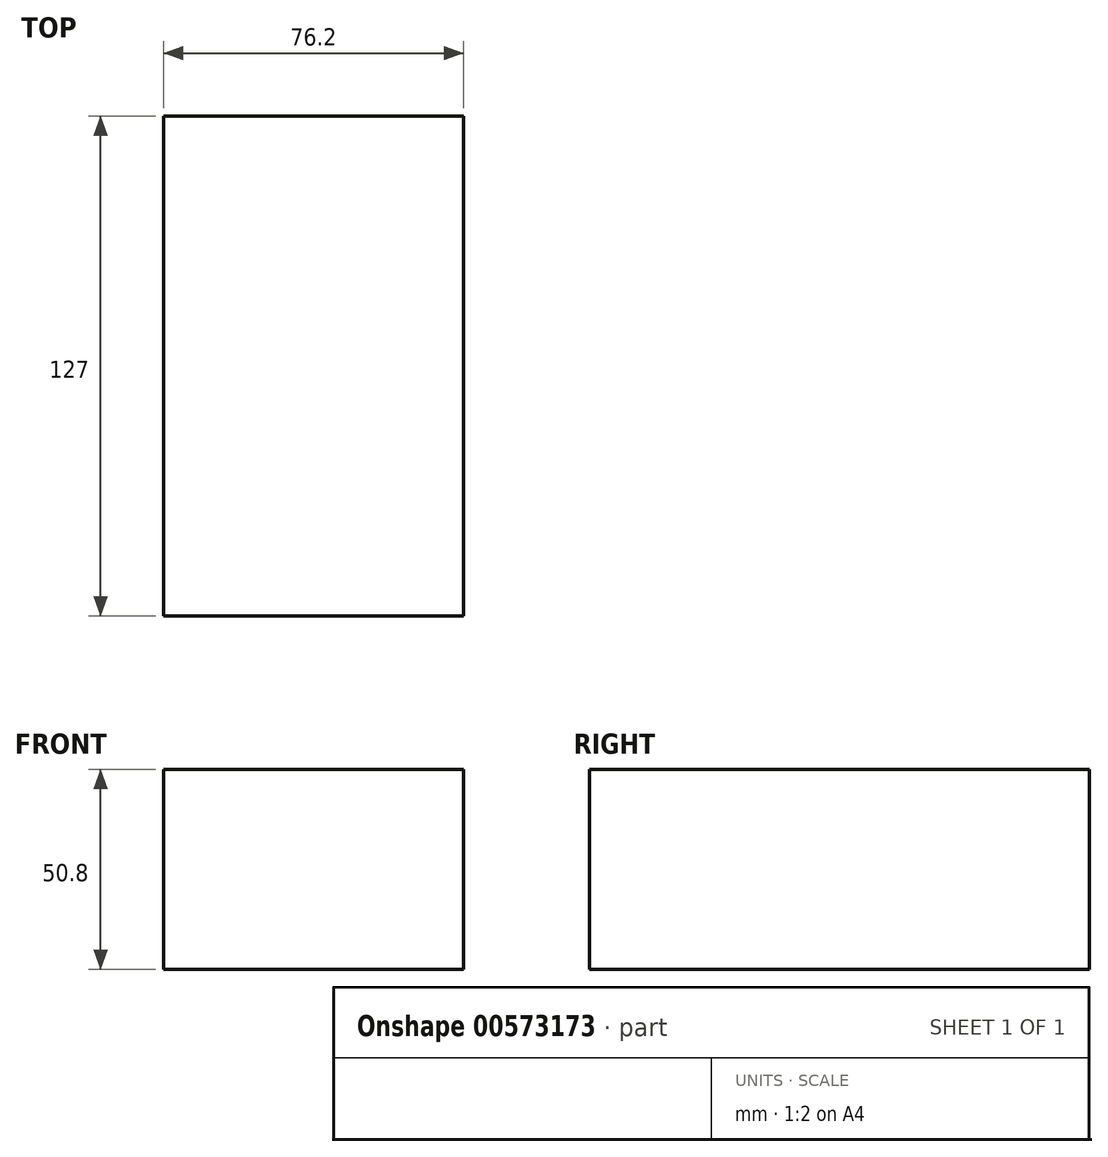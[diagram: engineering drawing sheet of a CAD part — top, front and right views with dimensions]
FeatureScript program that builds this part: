
annotation { "Feature Type Name" : "Feature", "Feature Type Description" : "" }
export const myFeature = defineFeature(function(context is Context, id is Id, definition is map)
    precondition{}
    {
        {
            var Q0;
            Q0=qCreatedBy(makeId("Top.planeOp"),FACE);
            var sketch = newSketch(context, id + "F0", { "sketchPlane" : qUnion([Q0])});
            skLineSegment(sketch, "E0.bottom", {"start": v(-28.82, -74.4) * mm, "end": v(47.38, -74.4) * mm});
            skLineSegment(sketch, "E0.top", {"start": v(-28.82, 52.6) * mm, "end": v(47.38, 52.6) * mm});
            skLineSegment(sketch, "E0.left", {"start": v(-28.82, -74.4) * mm, "end": v(-28.82, 52.6) * mm});
            skLineSegment(sketch, "E0.right", {"start": v(47.38, -74.4) * mm, "end": v(47.38, 52.6) * mm});
            skSolve(sketch);
        }
        {
            var Q0;
            Q0 = qSketchRegion(id + "F0", true);
            extrude(context, id + "F1", {"entities" : qUnion([Q0]), "depth" : 50.8 * mm, "offsetDistance" : 25.4 * mm});
        }
    });
